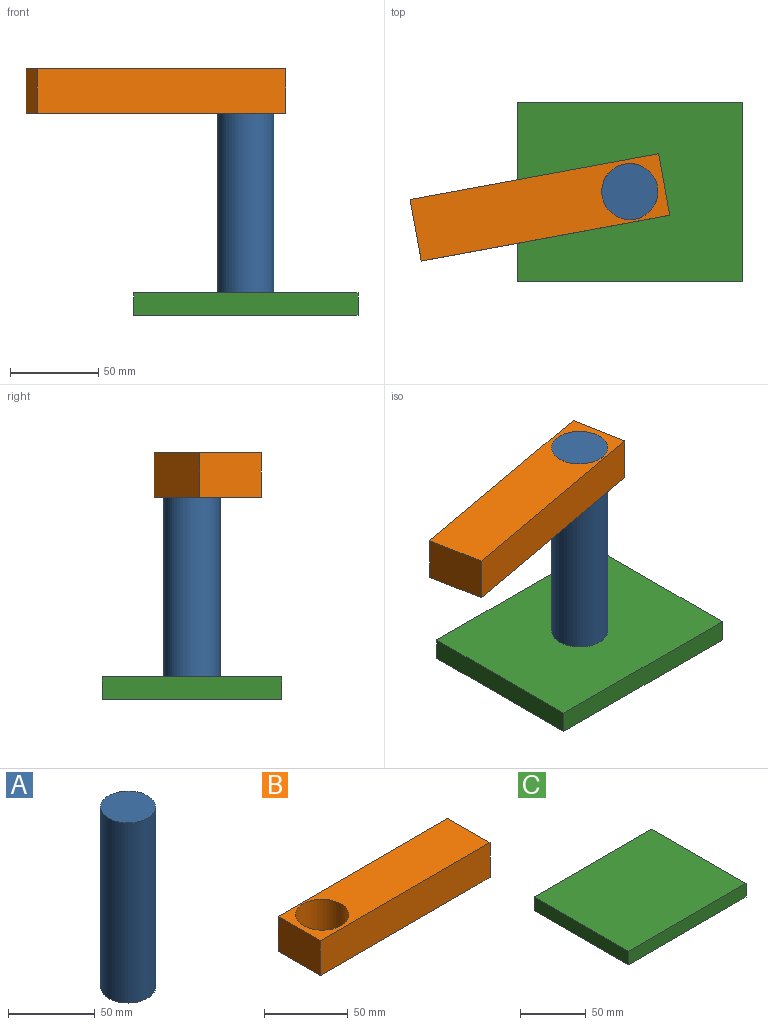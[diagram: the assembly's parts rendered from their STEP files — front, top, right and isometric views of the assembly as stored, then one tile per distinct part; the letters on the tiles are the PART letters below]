
ASSEMBLY  parts=3 mates=2
PART A: 3 faces, bbox 31.8x31.8x127 mm
  f0: cylinder r=15.89mm len=127mm, axis (0,0,-1), area 12680mm2, adj f1,f2
  f1: plane 31.78x31.78mm, normal (0,0,1), area 793.3mm2, adj f0
  f2: plane 31.78x31.78mm, normal (0,0,-1), area 793.3mm2, adj f0
PART B: 7 faces, bbox 143.1x35.4x25.4 mm
  f0: plane 35.41x25.4mm, normal (-1,0,0), area 899.4mm2, adj f1,f4,f5,f6
  f1: plane 143.07x25.4mm, normal (0,-1,0), area 3634mm2, adj f0,f2,f5,f6
  f2: plane 35.41x25.4mm, normal (1,0,0), area 899.4mm2, adj f1,f4,f5,f6
  f3: cylinder r=15.89mm len=31.78mm, axis (0,0,-1), area 2536mm2, adj f5,f6
  f4: plane 143.07x25.4mm, normal (0,1,0), area 3634mm2, adj f0,f2,f5,f6
  f5: plane 143.07x35.41mm, normal (0,0,1), area 4273.1mm2, adj f0,f1,f2,f3,f4
  f6: plane 143.07x35.41mm, normal (0,0,-1), area 4273.1mm2, adj f0,f1,f2,f3,f4
PART C: 6 faces, bbox 127x101.6x12.7 mm
  f0: plane 127x12.7mm, normal (0,-1,0), area 1612.9mm2, adj f1,f3,f4,f5
  f1: plane 101.6x12.7mm, normal (1,0,0), area 1290.3mm2, adj f0,f2,f4,f5
  f2: plane 127x12.7mm, normal (0,1,0), area 1612.9mm2, adj f1,f3,f4,f5
  f3: plane 101.6x12.7mm, normal (-1,0,0), area 1290.3mm2, adj f0,f2,f4,f5
  f4: plane 127x101.6mm, normal (0,0,1), area 12903.2mm2, adj f0,f1,f2,f3
  f5: plane 127x101.6mm, normal (0,0,-1), area 12903.2mm2, adj f0,f1,f2,f3
PLACE A t=(-5.03,27.38,-5.39)mm
PLACE B rot(axis=(0,0,-1),169.6deg) t=(-5.03,27.38,-30.79)mm
PLACE C t=(-5.03,27.38,-18.09)mm fixed
MATE revolute B.f3 <-> A.f0  axis (0,0,1) through (-5.03,27.38,121.61)mm
MATE fastened A.f0 <-> C.f4  axis (0,0,-1) through (-5.03,27.38,-5.39)mm
